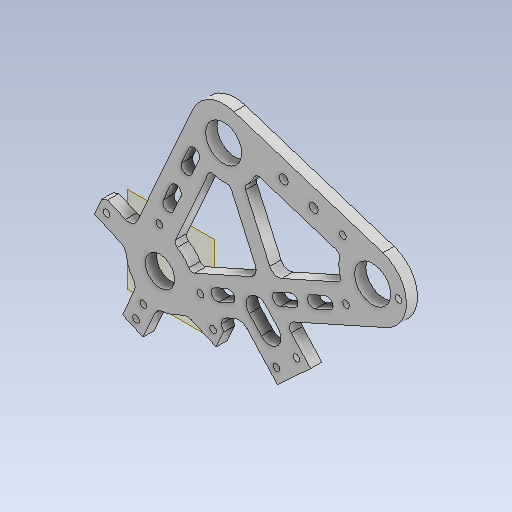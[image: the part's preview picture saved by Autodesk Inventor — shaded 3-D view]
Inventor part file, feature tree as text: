
AUTODESK INVENTOR PART (.ipt)
format: ipt  version: 2020 (Build 240168000, 168)  size: 718,336 bytes
history: native  units: mm
features: sketch x15, extrude x13, reference x12, projected_geometry x11, other x9, fillet x5, hole x2, plane x1, chamfer x1
ambient origin geometry x8: Origin, YZ Plane, XZ Plane, XY Plane, X Axis, Y Axis, Z Axis, Center Point
bodies: Solid1 (feature_tree)
feature tree (69):
  plane  "Work Plane1"
  extrude  "Extrusion1"  Depth=30.0mm
  extrude  "Extrusion2"  Depth=30.0mm
  hole  "Hole1"  [1 undecoded]
  extrude  "Extrusion3"  Depth=5.0mm TaperAngle=0.0deg
  extrude  "Extrusion4"  Depth=17.0mm
  chamfer  "Chamfer1"  Distance=5.0mm
  extrude  "Extrusion5"  Depth=10.0mm
  fillet  "Fillet1"  Radius=7.5mm
  extrude  "Extrusion6"  Depth=5.0mm TaperAngle=0.0deg
  extrude  "Extrusion7"  Depth=3.0mm
  extrude  "Extrusion8"  Depth=3.0mm
  extrude  "Extrusion9"  Depth=4.0mm
  extrude  "Extrusion10"  Depth=7.0mm
  hole  "Hole2"  [1 undecoded]
  fillet  "Fillet2"  Radius=4.0mm
  fillet  "Fillet3"  Radius=5.0mm
  fillet  "Fillet4"  Radius=16.0mm
  fillet  "Fillet5"  Radius=16.0mm
  extrude  "Extrusion11"  Depth=10.0mm
  extrude  "Extrusion12"  Depth=10.0mm
  extrude  "Extrusion13"  Depth=10.0mm
  sketch  "Sketch1"  dims[d0=30.0mm d1=30.0mm]
  reference  "Reference1"
  reference  "Reference2"
  reference  "Reference3"
  sketch  "Sketch2"  dims[d2=30.0mm d3=30.0mm]
  reference  "Reference4"
  projected_geometry  "Projected Loop1"
  sketch  "Sketch3"  dims[d4=30.0mm d5=30.0mm]
  reference  "Reference5"
  reference  "Reference6"
  sketch  "Sketch4"  dims[d6=5.0mm d7=0.0mm d8=5.0mm d9=0.0mm]
  reference  "Reference7"
  projected_geometry  "Projected Loop2"
  sketch  "Sketch5"  dims[d10=3.0mm d11=6.0mm d12=4.0mm d13=2.0mm d14=90.0deg d15=17.0mm d16=0.0mm d17=7.5mm]
  reference  "Reference8"
  reference  "Reference9"
  reference  "Reference10"
  projected_geometry  "Projected Loop3"
  sketch  "Sketch6"  dims[d18=10.0mm d19=5.0mm d20=0.0mm]
  projected_geometry  "Projected Loop4"
  sketch  "Sketch7"  dims[d21=7.5mm d22=10.0mm d23=7.5mm]
  projected_geometry  "Projected Loop5"
  sketch  "Sketch8"  dims[d24=10.0mm d25=5.0mm d26=0.0mm]
  reference  "Reference11"
  reference  "Reference12"
  sketch  "Sketch9"  dims[d27=2.0mm d28=2.0mm d29=45.0deg d30=3.0mm]
  projected_geometry  "Projected Loop6"
  sketch  "Sketch10"  dims[d31=3.0mm d32=3.0mm]
  sketch  "Sketch11"  dims[d33=5.0mm d34=0.0mm d35=4.0mm]
  projected_geometry  "Projected Loop7"
  sketch  "Sketch12"  dims[d36=7.0mm d37=50.0mm]
  projected_geometry  "Projected Loop8"
  sketch  "Sketch13"  dims[d38=5.0mm d39=0.0mm d40=4.0mm d41=4.0mm d42=5.0mm d43=0.0mm d44=16.0mm d45=16.0mm]
  projected_geometry  "Projected Loop9"
  sketch  "Sketch14"  dims[d46=10.0mm d47=0.0mm d48=13.0mm]
  projected_geometry  "Projected Loop10"
  sketch  "Sketch15"  dims[d49=10.0mm d50=0.0mm d51=18.0mm d52=18.0mm d53=3.0mm d54=3.0mm d55=11.5mm d56=3.0mm d57=4.363323mm d58=4.363323mm d59=10.0mm d60=0.0mm d61=18.0mm d62=18.0mm d63=18.0mm d64=27.052603mm d65=20.071286mm d66=3.0mm d67=6.0mm d68=4.0mm d69=2.0mm d70=90.0deg d71=17.0mm d72=0.0mm d73=2.0mm d74=4.0mm d75=3.0mm d76=5.0mm d77=15.0mm d78=4.0mm d79=10.0mm d80=10.0mm d81=0.0mm d82=8.0mm d83=6.0mm d84=5.0mm d85=9.0mm d86=7.0mm d87=5.0mm d88=10.0mm d89=7.0mm d90=5.0mm d91=10.0mm d92=0.0mm d93=10.0mm d94=8.0mm d95=5.0mm d96=12.0mm d97=8.0mm d98=5.0mm d99=10.0mm d100=0.0mm]
  projected_geometry  "Projected Loop11"
  parser-record x1  (decoder bookkeeping rows leaked as tree rows — omitted from the tree; the rows remain in map.json)
  other  "reducer_1.iam"
  other  "xl_20:1"
  other  "xl_wheel_ass:1"
  other  "xl_60_ori:1"
  other  "xl_60_out:1"
  other  "slide_holder_1:1"
  other  "motor_holder_7:1"
  other  "slide_holder_2:1"
note: 2 required parameter values undecoded (feature->parameter linkage not recoverable at this tier; creation-order binding heuristic only, values carry confidence <= 0.55)
note: 1 file-system path scrubbed to <path> (originals preserved in map.json)
